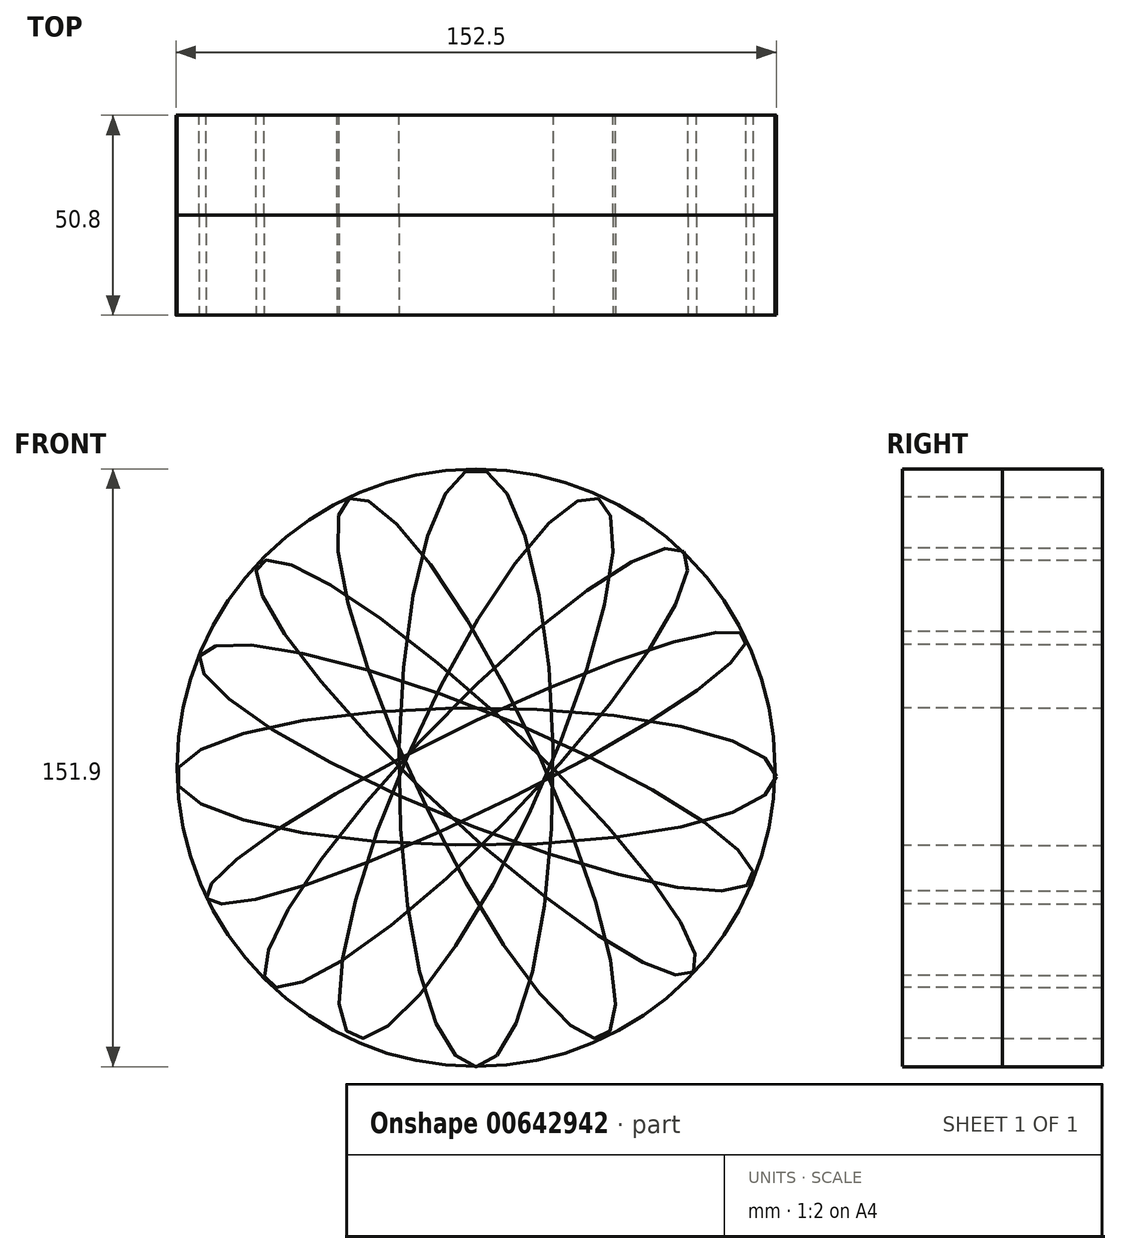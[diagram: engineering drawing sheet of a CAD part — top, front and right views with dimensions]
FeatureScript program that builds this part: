
annotation { "Feature Type Name" : "Feature", "Feature Type Description" : "" }
export const myFeature = defineFeature(function(context is Context, id is Id, definition is map)
    precondition{}
    {
        {
            var Q0;
            Q0=qCreatedBy(makeId("Front.planeOp"),FACE);
            var sketch = newSketch(context, id + "F0", { "sketchPlane" : qUnion([Q0])});
            skCircle(sketch, "E0", {"center": v(0, 0) * mm, "radius": 75.94 * mm});
            skEllipse(sketch, "E1", {"center": v(0, 0) * mm, "majorRadius": 75.75 * mm, "minorRadius": 13.5 * mm, "majorAxis": v(0.73, -0.68)});
            skEllipse(sketch, "E2", {"center": v(0, 0) * mm, "majorRadius": 76.16 * mm, "minorRadius": 14.93 * mm, "majorAxis": v(0.7, 0.72)});
            skEllipse(sketch, "E3", {"center": v(0, 0) * mm, "majorRadius": 75.95 * mm, "minorRadius": 19.6 * mm, "majorAxis": v(0, -1)});
            skEllipse(sketch, "E4", {"center": v(0, -2.26) * mm, "majorRadius": 76.25 * mm, "minorRadius": 17.44 * mm, "majorAxis": v(1, 0)});
            skEllipse(sketch, "E5", {"center": v(0, 0) * mm, "majorRadius": 75.18 * mm, "minorRadius": 17.15 * mm, "majorAxis": v(0.41, 0.91)});
            skEllipse(sketch, "E6", {"center": v(0, 0) * mm, "majorRadius": 76.07 * mm, "minorRadius": 10.81 * mm, "majorAxis": v(-0.9, -0.44)});
            skEllipse(sketch, "E7", {"center": v(0, 0) * mm, "majorRadius": 75.77 * mm, "minorRadius": 14.22 * mm, "majorAxis": v(-0.93, 0.38)});
            skEllipse(sketch, "E8", {"center": v(0, 0) * mm, "majorRadius": 75.68 * mm, "minorRadius": 15.78 * mm, "majorAxis": v(-0.43, 0.9)});
            skSolve(sketch);
        }
        {
            var Q0;
            Q0=sQuery(id+"F0.wireOp",EDGE,"E2");
            extrude(context, id + "F1", {"bodyType" : ToolBodyType.SURFACE, "surfaceEntities" : qUnion([Q0]), "depth" : 25.4 * mm, "offsetDistance" : 25.4 * mm});
        }
        {
            var Q0;
            Q0=sQuery(id+"F0.wireOp",EDGE,"E5");
            extrude(context, id + "F2", {"bodyType" : ToolBodyType.SURFACE, "surfaceEntities" : qUnion([Q0]), "depth" : 25.4 * mm, "offsetDistance" : 25.4 * mm});
        }
        {
            var Q0;
            Q0=sQuery(id+"F0.wireOp",EDGE,"E3");
            extrude(context, id + "F3", {"bodyType" : ToolBodyType.SURFACE, "surfaceEntities" : qUnion([Q0]), "depth" : 25.4 * mm, "offsetDistance" : 25.4 * mm});
        }
        {
            var Q0;
            Q0=sQuery(id+"F0.wireOp",EDGE,"E8");
            extrude(context, id + "F4", {"bodyType" : ToolBodyType.SURFACE, "surfaceEntities" : qUnion([Q0]), "depth" : 25.4 * mm, "offsetDistance" : 25.4 * mm});
        }
        {
            var Q0;
            Q0=sQuery(id+"F0.wireOp",EDGE,"E6");
            extrude(context, id + "F5", {"bodyType" : ToolBodyType.SURFACE, "surfaceEntities" : qUnion([Q0]), "depth" : 25.4 * mm, "offsetDistance" : 25.4 * mm});
        }
        {
            var Q0;
            Q0=sQuery(id+"F0.wireOp",EDGE,"E4");
            extrude(context, id + "F6", {"bodyType" : ToolBodyType.SURFACE, "surfaceEntities" : qUnion([Q0]), "depth" : 25.4 * mm, "offsetDistance" : 25.4 * mm});
        }
        {
            var Q0;
            Q0=sQuery(id+"F0.wireOp",EDGE,"E1");
            extrude(context, id + "F7", {"bodyType" : ToolBodyType.SURFACE, "surfaceEntities" : qUnion([Q0]), "depth" : 25.4 * mm, "offsetDistance" : 25.4 * mm});
        }
        {
            var Q0;
            Q0=sQuery(id+"F0.wireOp",EDGE,"E7");
            extrude(context, id + "F8", {"bodyType" : ToolBodyType.SURFACE, "surfaceEntities" : qUnion([Q0]), "depth" : 25.4 * mm, "offsetDistance" : 25.4 * mm});
        }
        {
            var Q0;
            Q0=sQuery(id+"F0.wireOp",EDGE,"E0");
            extrude(context, id + "F9", {"bodyType" : ToolBodyType.SURFACE, "surfaceEntities" : qUnion([Q0]), "depth" : 25.4 * mm, "offsetDistance" : 25.4 * mm});
        }
        {
            var Q0;
            Q0=makeQuery(id+"F9.opExtrude","SWEPT_BODY",BODY,{"disambiguationData":[OSD([sQuery(id+"F0.wireOp",EDGE,"E0")])]});
            var Q1;
            Q1=makeQuery(id+"F8.opExtrude","SWEPT_BODY",BODY,{"disambiguationData":[OSD([sQuery(id+"F0.wireOp",EDGE,"E7")])]});
            var Q2;
            Q2=makeQuery(id+"F5.opExtrude","SWEPT_BODY",BODY,{"disambiguationData":[OSD([sQuery(id+"F0.wireOp",EDGE,"E6")])]});
            var Q3;
            Q3=makeQuery(id+"F2.opExtrude","SWEPT_BODY",BODY,{"disambiguationData":[OSD([sQuery(id+"F0.wireOp",EDGE,"E5")])]});
            var Q4;
            Q4=makeQuery(id+"F7.opExtrude","SWEPT_BODY",BODY,{"disambiguationData":[OSD([sQuery(id+"F0.wireOp",EDGE,"E1")])]});
            var Q5;
            Q5=makeQuery(id+"F1.opExtrude","SWEPT_BODY",BODY,{"disambiguationData":[OSD([sQuery(id+"F0.wireOp",EDGE,"E2")])]});
            var Q6;
            Q6=makeQuery(id+"F3.opExtrude","SWEPT_BODY",BODY,{"disambiguationData":[OSD([sQuery(id+"F0.wireOp",EDGE,"E3")])]});
            var Q7;
            Q7=makeQuery(id+"F6.opExtrude","SWEPT_BODY",BODY,{"disambiguationData":[OSD([sQuery(id+"F0.wireOp",EDGE,"E4")])]});
            var Q8;
            Q8=qCreatedBy(makeId("Front.planeOp"),FACE);
            mirror(context, id + "F10", {"entities" : qUnion([Q0, Q1, Q2, Q3, Q4, Q5, Q6, Q7]), "mirrorPlane" : qUnion([Q8])});
        }
        {
            var Q0;
            Q0=makeQuery(id+"F4.opExtrude","SWEPT_BODY",BODY,{"disambiguationData":[OSD([sQuery(id+"F0.wireOp",EDGE,"E8")])]});
            var Q1;
            Q1=qCreatedBy(makeId("Front.planeOp"),FACE);
            mirror(context, id + "F11", {"entities" : qUnion([Q0]), "mirrorPlane" : qUnion([Q1])});
        }
    });
